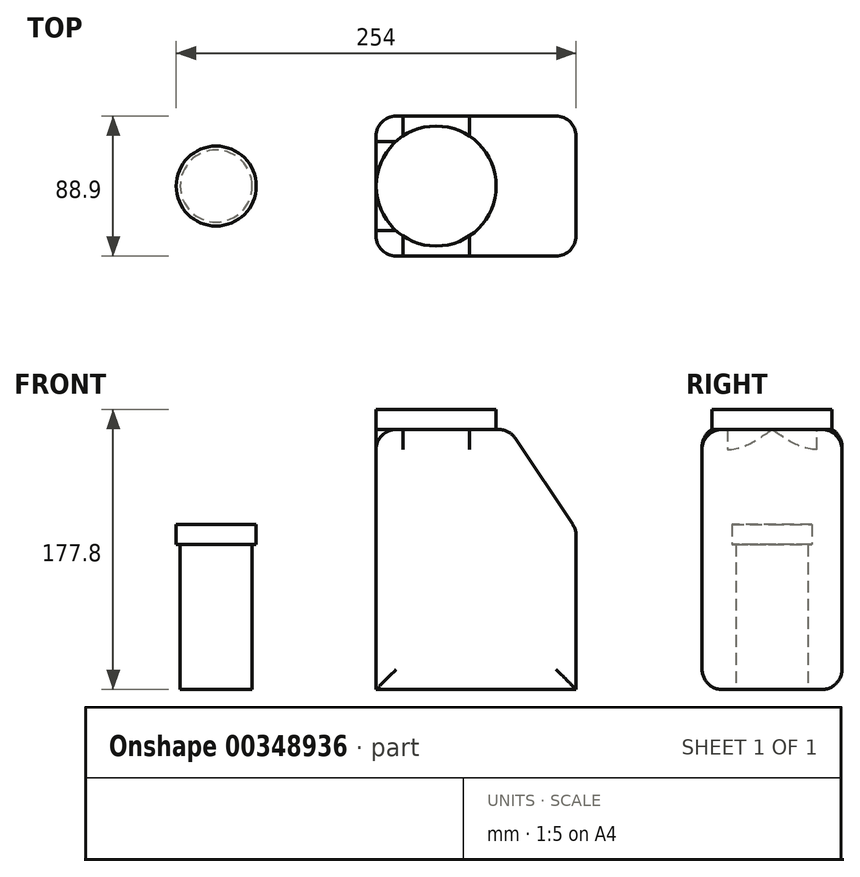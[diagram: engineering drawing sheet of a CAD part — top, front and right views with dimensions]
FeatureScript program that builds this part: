
annotation { "Feature Type Name" : "Feature", "Feature Type Description" : "" }
export const myFeature = defineFeature(function(context is Context, id is Id, definition is map)
    precondition{}
    {
        {
            var Q0;
            Q0=qCreatedBy(makeId("Front.planeOp"),FACE);
            var sketch = newSketch(context, id + "F0", { "sketchPlane" : qUnion([Q0])});
            skLineSegment(sketch, "E0.bottom", {"start": v(0, 0) * mm, "end": v(22.86, 0) * mm});
            skLineSegment(sketch, "E0.top", {"start": v(0, 104.78) * mm, "end": v(25.4, 104.78) * mm});
            skLineSegment(sketch, "E0.left", {"start": v(0, 0) * mm, "end": v(0, 104.78) * mm});
            skLineSegment(sketch, "E0.right", {"start": v(22.86, 0) * mm, "end": v(22.86, 92.08) * mm});
            skLineSegment(sketch, "E1.top", {"start": v(22.86, 92.08) * mm, "end": v(25.4, 92.08) * mm});
            skLineSegment(sketch, "E1.right", {"start": v(25.4, 104.78) * mm, "end": v(25.4, 92.08) * mm});
            skSolve(sketch);
        }
        {
            var Q0;
            Q0 = qSketchRegion(id + "F0", true);
            var Q1;
            Q1=sQuery(id+"F0.wireOp",EDGE,"E0.left");
            revolve(context, id + "F1", {"entities" : qUnion([Q0]), "axis" : qUnion([Q1]), "revolveType" : RevolveType.FULL});
        }
        {
            var Q0;
            Q0=qCreatedBy(makeId("Front.planeOp"),FACE);
            var sketch = newSketch(context, id + "F2", { "sketchPlane" : qUnion([Q0])});
            skLineSegment(sketch, "E2.bottom", {"start": v(101.6, 0) * mm, "end": v(228.6, 0) * mm});
            skLineSegment(sketch, "E2.top", {"start": v(101.6, 177.8) * mm, "end": v(177.8, 177.8) * mm});
            skLineSegment(sketch, "E2.left", {"start": v(101.6, 0) * mm, "end": v(101.6, 177.8) * mm});
            skLineSegment(sketch, "E2.right", {"start": v(228.6, 0) * mm, "end": v(228.6, 101.6) * mm});
            skLineSegment(sketch, "E3", {"start": v(177.8, 177.8) * mm, "end": v(228.6, 101.6) * mm});
            skSolve(sketch);
        }
        {
            var Q0;
            Q0 = qSketchRegion(id + "F2", true);
            extrude(context, id + "F3", {"entities" : qUnion([Q0]), "endBound" : BoundingType.SYMMETRIC, "depth" : 88.9 * mm});
        }
        {
            var Q0;
            Q0=makeQuery(id+"F3.opExtrude","SWEPT_FACE",FACE,{"disambiguationData":[OSD([sQuery(id+"F2.wireOp",EDGE,"E2.top")])]});
            var sketch = newSketch(context, id + "F4", { "sketchPlane" : qUnion([Q0])});
            skCircle(sketch, "E4", {"center": v(139.7, 0) * mm, "radius": 38.1 * mm});
            skPoint(sketch, "E4.centerSnap0", {"position": v(139.7, 44.45) * mm});
            skPoint(sketch, "E4.centerSnap1", {"position": v(177.8, 0) * mm});
            skCircle(sketch, "E5", {"center": v(139.7, 0) * mm, "radius": 153.08 * mm});
            skSolve(sketch);
        }
        {
            var Q0;
            Q0 = qSketchRegion(id + "F4", true);
            extrude(context, id + "F5", {"entities" : qUnion([Q0]), "operationType" : NewBodyOperationType.REMOVE, "oppositeDirection" : true, "depth" : 12.7 * mm});
        }
        {
            var Q0;
            Q0=makeQuery(id+"F5.boolean.opBoolean","INTERSECT",EDGE,{"derivedFrom":[makeQuery(id+"F3.opExtrude","CAP_FACE",FACE,{"disambiguationData":[OSD([sQuery(id+"F2.wireOp",EDGE,"E2.bottom"),sQuery(id+"F2.wireOp",EDGE,"E2.top"),sQuery(id+"F2.wireOp",EDGE,"E2.left"),sQuery(id+"F2.wireOp",EDGE,"E2.right"),sQuery(id+"F2.wireOp",EDGE,"E3")])],"isStart":false}),makeQuery(id+"F5.opExtrude","CAP_FACE",FACE,{"disambiguationData":[OSD([sQuery(id+"F4.wireOp",EDGE,"E4"),sQuery(id+"F4.wireOp",EDGE,"E5")])],"isStart":false})]});
            var Q1;
            Q1=makeQuery(id+"F5.boolean.opBoolean","INTERSECT",EDGE,{"derivedFrom":[makeQuery(id+"F3.opExtrude","SWEPT_FACE",FACE,{"disambiguationData":[OSD([sQuery(id+"F2.wireOp",EDGE,"E3")])]}),makeQuery(id+"F5.opExtrude","CAP_FACE",FACE,{"disambiguationData":[OSD([sQuery(id+"F4.wireOp",EDGE,"E4"),sQuery(id+"F4.wireOp",EDGE,"E5")])],"isStart":false})]});
            var Q2;
            Q2=makeQuery(id+"F5.boolean.opBoolean","INTERSECT",EDGE,{"derivedFrom":[makeQuery(id+"F3.opExtrude","CAP_FACE",FACE,{"disambiguationData":[OSD([sQuery(id+"F2.wireOp",EDGE,"E2.bottom"),sQuery(id+"F2.wireOp",EDGE,"E2.top"),sQuery(id+"F2.wireOp",EDGE,"E2.left"),sQuery(id+"F2.wireOp",EDGE,"E2.right"),sQuery(id+"F2.wireOp",EDGE,"E3")])],"isStart":true}),makeQuery(id+"F5.opExtrude","CAP_FACE",FACE,{"disambiguationData":[OSD([sQuery(id+"F4.wireOp",EDGE,"E4"),sQuery(id+"F4.wireOp",EDGE,"E5")])],"isStart":false})]});
            var Q3;
            Q3=makeQuery(id+"F5.boolean.opBoolean","INTERSECT",EDGE,{"disambiguationData":[OD(0.0)],"derivedFrom":[makeQuery(id+"F3.opExtrude","SWEPT_FACE",FACE,{"disambiguationData":[OSD([sQuery(id+"F2.wireOp",EDGE,"E2.left")])]}),makeQuery(id+"F5.opExtrude","CAP_FACE",FACE,{"disambiguationData":[OSD([sQuery(id+"F4.wireOp",EDGE,"E4"),sQuery(id+"F4.wireOp",EDGE,"E5")])],"isStart":false})]});
            var Q4;
            Q4=makeQuery(id+"F3.opExtrude","CAP_EDGE",EDGE,{"disambiguationData":[OSD([sQuery(id+"F2.wireOp",EDGE,"E2.left")])],"isStart":true});
            var Q5;
            Q5=makeQuery(id+"F3.opExtrude","CAP_EDGE",EDGE,{"disambiguationData":[OSD([sQuery(id+"F2.wireOp",EDGE,"E2.left")])],"isStart":false});
            var Q6;
            Q6=makeQuery(id+"F3.opExtrude","CAP_EDGE",EDGE,{"disambiguationData":[OSD([sQuery(id+"F2.wireOp",EDGE,"E3")])],"isStart":true});
            var Q7;
            Q7=makeQuery(id+"F3.opExtrude","CAP_EDGE",EDGE,{"disambiguationData":[OSD([sQuery(id+"F2.wireOp",EDGE,"E3")])],"isStart":false});
            var Q8;
            Q8=makeQuery(id+"F3.opExtrude","SWEPT_EDGE",EDGE,{"disambiguationData":[OSD([sQuery(id+"F2.wireOp",EDGE,"E2.right"),sQuery(id+"F2.wireOp",EDGE,"E3")])]});
            var Q9;
            Q9=makeQuery(id+"F3.opExtrude","CAP_EDGE",EDGE,{"disambiguationData":[OSD([sQuery(id+"F2.wireOp",EDGE,"E2.right")])],"isStart":false});
            var Q10;
            Q10=makeQuery(id+"F3.opExtrude","CAP_FACE",FACE,{"disambiguationData":[OSD([sQuery(id+"F2.wireOp",EDGE,"E2.bottom"),sQuery(id+"F2.wireOp",EDGE,"E2.top"),sQuery(id+"F2.wireOp",EDGE,"E2.left"),sQuery(id+"F2.wireOp",EDGE,"E2.right"),sQuery(id+"F2.wireOp",EDGE,"E3")])],"isStart":true});
            var Q11;
            Q11=makeQuery(id+"F3.opExtrude","CAP_EDGE",EDGE,{"disambiguationData":[OSD([sQuery(id+"F2.wireOp",EDGE,"E2.bottom")])],"isStart":false});
            fillet(context, id + "F6", {"entities" : qUnion([Q0, Q1, Q2, Q3, Q4, Q5, Q6, Q7, Q8, Q9, Q10, Q11]), "radius" : 12.7 * mm, "tangentPropagation" : true, "allowEdgeOverflow" : false});
        }
    });
